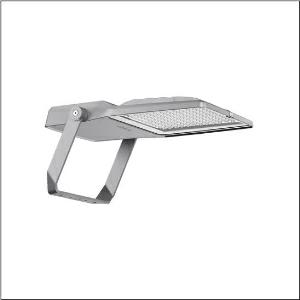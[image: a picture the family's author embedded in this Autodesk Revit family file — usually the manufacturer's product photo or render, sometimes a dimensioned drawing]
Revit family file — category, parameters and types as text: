
# Revit family: floodlight_fl_21_iq_midi___rs12_5xa7781e2b1a_85c8
name_source: partatom
category: Lighting Fixtures
units: mm (PartAtom-declared; Revit-internal decimal feet)

## family parameters
Cut with Voids When Loaded = No
Host = Face
Light Source = No
Part Type = Normal
Room Calculation Point = No
Round Connector Dimension = Use Diameter
Shared = No

## types (1)
- --- (1 x LED, 26730 lm, 208.1 W, 3000K)
    Apparent Load = 208 VA
    CIE Flux Codes = 79 92 99 100 100
    Color Rendering = 70
    Color Temperature = 3000K
    Default Elevation = 1800 mm
    Description = Floodlight FL 21 iQ midi, floodlight, primary light control with lens, of PMMA, primary optical cover: protective disc, of toughened safety glass, transparent, light distribution: RS12, light emission: direct distribution, installation type: surface-mounted, LED, High Power LED, rated luminous flux: 26.730lm, luminous efficacy: 128lm/W, light colour: 730, colour temperature: 3000K, control gear: ECG iQ, control: optimised constant luminous flux control (CLO 2.0), Desk-Remote (wireless, voltage-free reading and setting of iQ features in the workshop via application-optimized NFC function/RFID function), Light-Fading, Smart-Wire, Night-Set, Lumen-Switch, Temp-Guard, Auto-Match, with terminal, 6-pole, mains connection: 220..240V, AC, 50/60Hz, start of lifetime: 208W, end of service life: 227W, reduction: 90W, luminaire housing, of diecast aluminium, powder-coated, Siteco® metallic grey (DB 702S), corrosivity category C5 mid according to DIN EN ISO 12944, sealing non-destructively replaceable, mounting bracket, of steel, galvanised, powder-coated, Siteco® metallic grey (DB 702S), protection rating (complete): IP66, insulation class (complete): insulation class II (safety insulation), certification: CE, protection symbol: D, impact resistance: IK08, permissible operating ambient temperature: -40..+40°C, permissible operating ambient temperature for outdoor applications: -40..+50°C, standard: DIN EN 12944, LABS conformity tested according to VDMA 24364:2018-05, packaging unit: 1 piece

Light Distribution: RS12
    Height = 76 mm
    Lamp = 1 x LED
    Lamp Light Flux = 26730 lm
    Lamp Power = 208.1 W
    Lamp count = 1
    Length = 657 mm
    Luminous efficacy = 128 lm/W
    Manufacturer = Siteco
    ModVariant = No
    Model = 5XA7781E2B1A
    Number of Poles = 1
    OnlyDefault = Yes
    Power Factor = 1
    Product Name = Floodlight FL 21 iQ midi | RS12
    Product group = floodlight | pylon annexe
    ProductGroupID = 6200
    Protection Class = Protection class II
    Protection Degree = IP 66
    RLX_Detail_Level = 1
    RLX_Emergency_Light_Flux = 0 lm
    RLX_Emergency_Type = 0
    RLX_Emergency_Type_DB = No
    RlxData = <blob elided: 141005 chars, md5=147ddf94>
    Socket = socket
    Standby Power = 0 W
    System Light Flux = 26730 lm
    System Power = 208 W
    Type Comments = factory setting: luminous flux: 100 % | dim-lin: 254 | 710 mA
    Type Image = l_1006876.jpg
    URL = http://relux.com
    VarID = @adj_038059
    Voltage = 0 V
    Weight = 0.00 kg
    Width = 442 mm

## geometry (parser evidence)
native form markers: Blend x4, Sweep x11
no freeform markers — native parametric forms only
